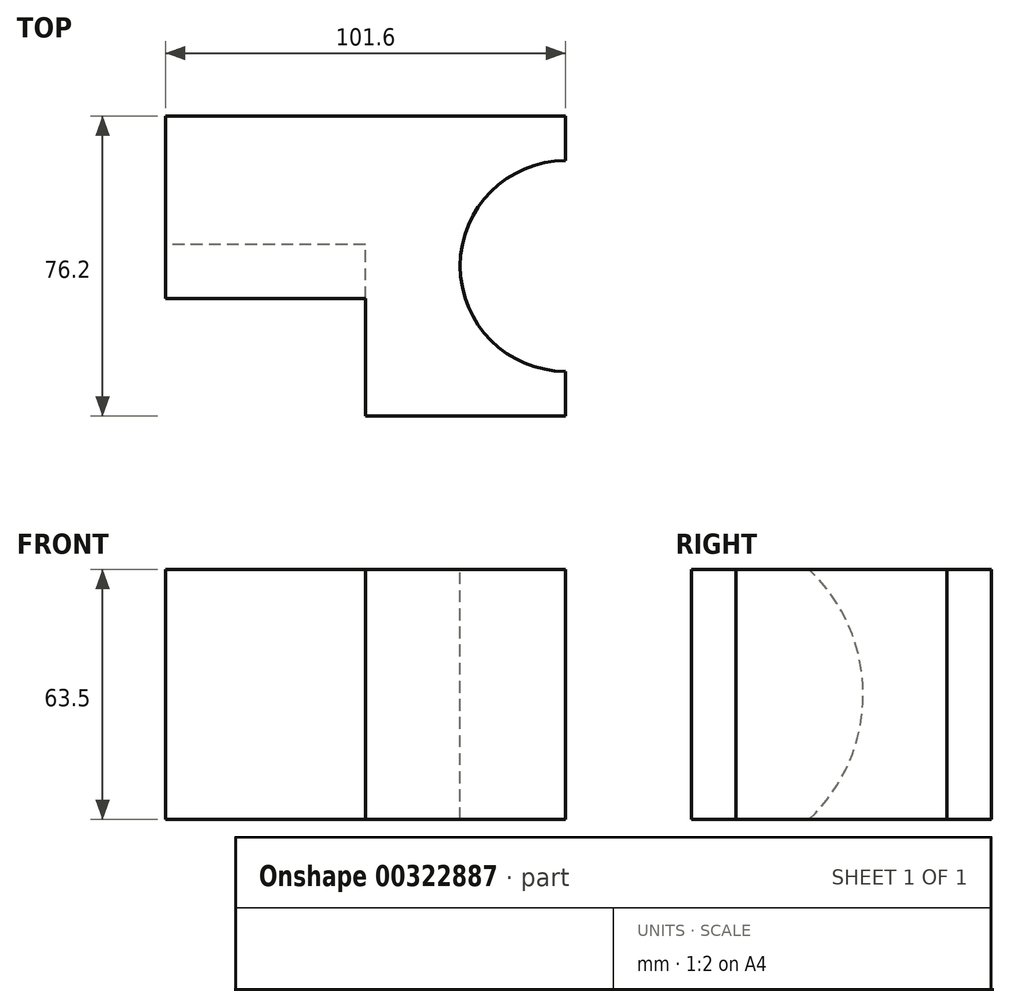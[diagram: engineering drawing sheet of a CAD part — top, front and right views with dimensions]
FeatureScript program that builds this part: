
annotation { "Feature Type Name" : "Feature", "Feature Type Description" : "" }
export const myFeature = defineFeature(function(context is Context, id is Id, definition is map)
    precondition{}
    {
        {
            var Q0;
            Q0=qCreatedBy(makeId("Top.planeOp"),FACE);
            var sketch = newSketch(context, id + "F0", { "sketchPlane" : qUnion([Q0])});
            skLineSegment(sketch, "E0.bottom", {"start": v(-49.82, 26.6) * mm, "end": v(51.78, 26.6) * mm});
            skLineSegment(sketch, "E0.top", {"start": v(-49.82, -49.6) * mm, "end": v(51.78, -49.6) * mm});
            skLineSegment(sketch, "E0.left", {"start": v(-49.82, 26.6) * mm, "end": v(-49.82, -49.6) * mm});
            skLineSegment(sketch, "E0.right", {"start": v(51.78, 26.6) * mm, "end": v(51.78, -49.6) * mm});
            skSolve(sketch);
        }
        {
            var Q0;
            Q0=makeQuery(id+"F0.imprint","IMPRINT",FACE,{"disambiguationData":[TD([[makeQuery(id+"F0.imprint","IMPRINT",EDGE,{"derivedFrom":sQuery(id+"F0.wireOp",EDGE,"E0.bottom")}),-1.0]])]});
            extrude(context, id + "F1", {"entities" : qUnion([Q0]), "depth" : 63.5 * mm});
        }
        {
            var Q0;
            Q0=makeQuery(id+"F1.opExtrude","CAP_FACE",FACE,{"disambiguationData":[OSD([sQuery(id+"F0.wireOp",EDGE,"E0.bottom"),sQuery(id+"F0.wireOp",EDGE,"E0.top"),sQuery(id+"F0.wireOp",EDGE,"E0.left"),sQuery(id+"F0.wireOp",EDGE,"E0.right")])],"isStart":false});
            var sketch = newSketch(context, id + "F2", { "sketchPlane" : qUnion([Q0])});
            skCircle(sketch, "E1", {"center": v(51.78, -11.5) * mm, "radius": 26.77 * mm});
            skSolve(sketch);
        }
        {
            var Q0;
            {var subQ0=sQuery(id+"F2.wireOp",EDGE,"E1");var subQ1=makeQuery(id+"F1.opExtrude","CAP_EDGE",EDGE,{"disambiguationData":[OSD([sQuery(id+"F0.wireOp",EDGE,"E0.right")])],"isStart":false});var subQ2=makeQuery(id+"F2.imprint","INTERSECT",VERTEX,{"disambiguationData":[OD(0.0)],"derivedFrom":[subQ1,subQ0]});Q0=makeQuery(id+"F2.imprint","IMPRINT",FACE,{"disambiguationData":[TD([[makeQuery(id+"F2.imprint","IMPRINT",EDGE,{"disambiguationData":[TD([[subQ2,-1.0]])],"derivedFrom":subQ0}),1.0]])]});}
            var Q1;
            {var subQ0=sQuery(id+"F2.wireOp",EDGE,"E1");var subQ1=makeQuery(id+"F1.opExtrude","CAP_EDGE",EDGE,{"disambiguationData":[OSD([sQuery(id+"F0.wireOp",EDGE,"E0.right")])],"isStart":false});var subQ2=makeQuery(id+"F2.imprint","INTERSECT",VERTEX,{"disambiguationData":[OD(0.0)],"derivedFrom":[subQ1,subQ0]});Q1=makeQuery(id+"F2.imprint","IMPRINT",FACE,{"disambiguationData":[TD([[makeQuery(id+"F2.imprint","IMPRINT",EDGE,{"disambiguationData":[TD([[subQ2,1.0]])],"derivedFrom":subQ0}),1.0]])]});}
            extrude(context, id + "F3", {"entities" : qUnion([Q0, Q1]), "operationType" : NewBodyOperationType.REMOVE, "endBound" : BoundingType.THROUGH_ALL, "oppositeDirection" : true, "depth" : 25.4 * mm});
        }
        {
            var Q0;
            Q0=makeQuery(id+"F1.opExtrude","SWEPT_FACE",FACE,{"disambiguationData":[OSD([sQuery(id+"F0.wireOp",EDGE,"E0.left")])]});
            var sketch = newSketch(context, id + "F4", { "sketchPlane" : qUnion([Q0])});
            skCircle(sketch, "E2", {"center": v(49.6, 31.75) * mm, "radius": 43.6 * mm});
            skSolve(sketch);
        }
        {
            var Q0;
            {var subQ1=sQuery(id+"F0.wireOp",EDGE,"E0.left");var subQ6=makeQuery(id+"F1.opExtrude","SWEPT_EDGE",EDGE,{"disambiguationData":[OSD([sQuery(id+"F0.wireOp",EDGE,"E0.top"),subQ1])]});Q0=makeQuery(id+"F4.imprint","IMPRINT",FACE,{"disambiguationData":[TD([[makeQuery(id+"F4.imprint","IMPRINT",EDGE,{"derivedFrom":subQ6}),1.0]])]});}
            var Q1;
            {var subQ1=sQuery(id+"F0.wireOp",EDGE,"E0.left");var subQ6=makeQuery(id+"F1.opExtrude","SWEPT_EDGE",EDGE,{"disambiguationData":[OSD([sQuery(id+"F0.wireOp",EDGE,"E0.top"),subQ1])]});Q1=makeQuery(id+"F4.imprint","IMPRINT",FACE,{"disambiguationData":[TD([[makeQuery(id+"F4.imprint","IMPRINT",EDGE,{"derivedFrom":subQ6}),-1.0]])]});}
            extrude(context, id + "F5", {"entities" : qUnion([Q0, Q1]), "operationType" : NewBodyOperationType.REMOVE, "oppositeDirection" : true, "depth" : 50.8 * mm});
        }
    });
